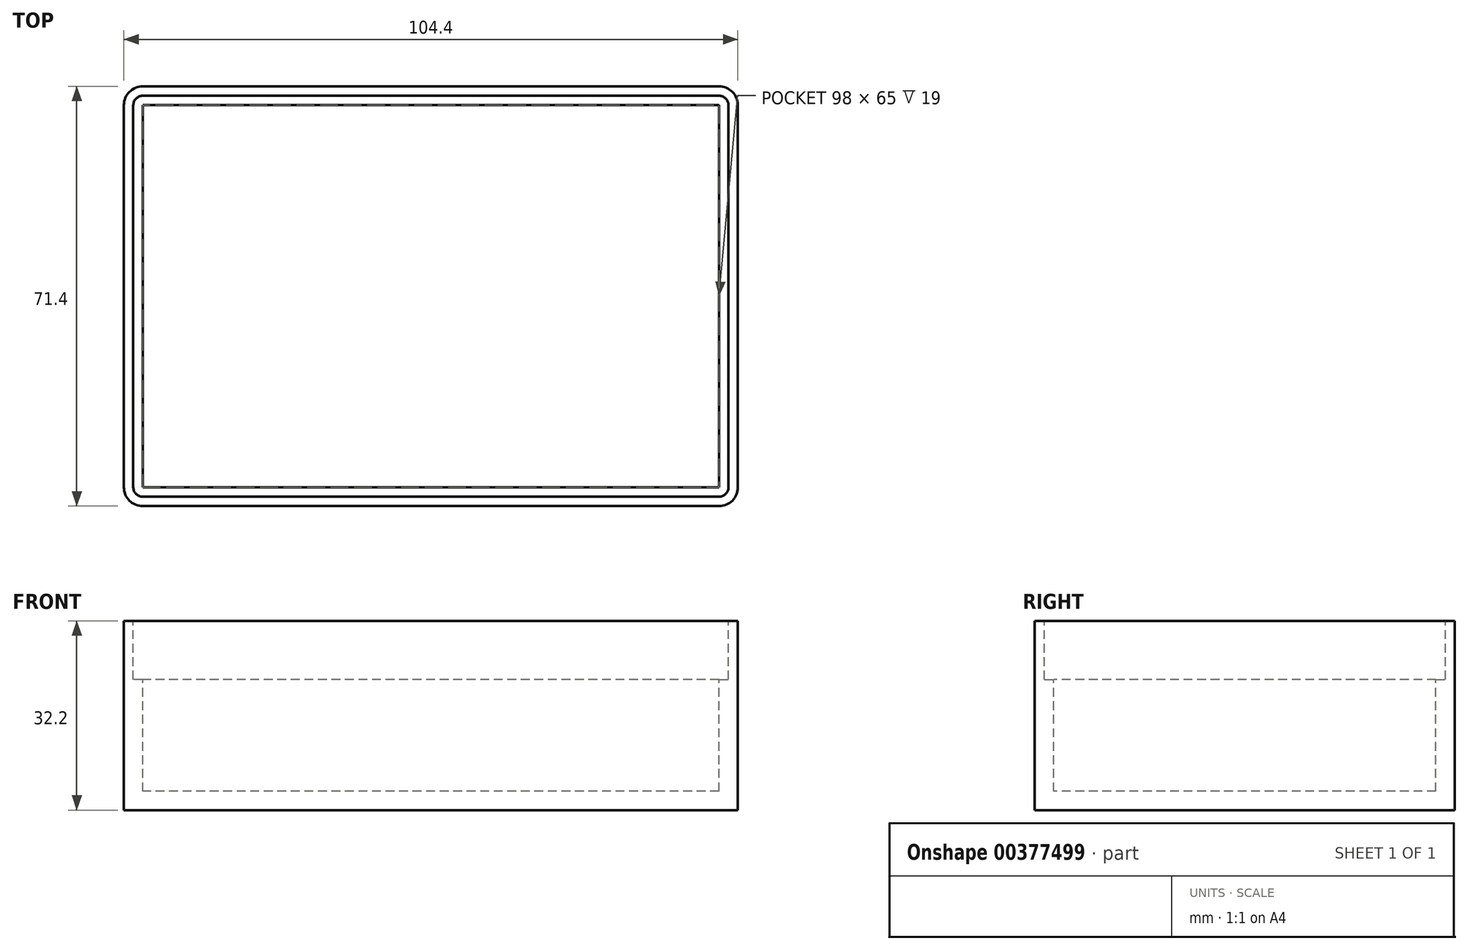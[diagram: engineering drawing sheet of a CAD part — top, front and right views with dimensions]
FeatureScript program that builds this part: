
annotation { "Feature Type Name" : "Feature", "Feature Type Description" : "" }
export const myFeature = defineFeature(function(context is Context, id is Id, definition is map)
    precondition{}
    {
        {
            assignVariable(context, id + "F0", {"name" : "InnerDepth", "anyValue" : 19 * mm});
        }
        {
            assignVariable(context, id + "F1", {"name" : "WallThickness", "anyValue" : 3.2 * mm});
        }
        {
            assignVariable(context, id + "F2", {"name" : "LidDepth", "anyValue" : 10 * mm});
        }
        {
            var Q0;
            Q0=qCreatedBy(makeId("Top.planeOp"),FACE);
            var sketch = newSketch(context, id + "F3", { "sketchPlane" : qUnion([Q0])});
            skLineSegment(sketch, "E0.bottom", {"start": v(52.2, 35.7) * mm, "end": v(-52.2, 35.7) * mm});
            skLineSegment(sketch, "E0.top", {"start": v(52.2, -35.7) * mm, "end": v(-52.2, -35.7) * mm});
            skLineSegment(sketch, "E0.left", {"start": v(52.2, 35.7) * mm, "end": v(52.2, -35.7) * mm});
            skLineSegment(sketch, "E0.right", {"start": v(-52.2, 35.7) * mm, "end": v(-52.2, -35.7) * mm});
            skPoint(sketch, "E0.middle", {"position": v(0, 0) * mm});
            skSolve(sketch);
        }
        {
            var Q0;
            Q0=qCreatedBy(makeId("Top.planeOp"),FACE);
            var sketch = newSketch(context, id + "F4", { "sketchPlane" : qUnion([Q0])});
            skLineSegment(sketch, "E1.bottom", {"start": v(50.6, 34.1) * mm, "end": v(-50.6, 34.1) * mm});
            skLineSegment(sketch, "E1.top", {"start": v(50.6, -34.1) * mm, "end": v(-50.6, -34.1) * mm});
            skLineSegment(sketch, "E1.left", {"start": v(50.6, 34.1) * mm, "end": v(50.6, -34.1) * mm});
            skLineSegment(sketch, "E1.right", {"start": v(-50.6, 34.1) * mm, "end": v(-50.6, -34.1) * mm});
            skPoint(sketch, "E1.middle", {"position": v(0, 0) * mm});
            skSolve(sketch);
        }
        {
            var Q0;
            Q0=qCreatedBy(makeId("Top.planeOp"),FACE);
            var sketch = newSketch(context, id + "F5", { "sketchPlane" : qUnion([Q0])});
            skLineSegment(sketch, "E2.bottom", {"start": v(49, 32.5) * mm, "end": v(-49, 32.5) * mm});
            skLineSegment(sketch, "E2.top", {"start": v(49, -32.5) * mm, "end": v(-49, -32.5) * mm});
            skLineSegment(sketch, "E2.left", {"start": v(49, 32.5) * mm, "end": v(49, -32.5) * mm});
            skLineSegment(sketch, "E2.right", {"start": v(-49, 32.5) * mm, "end": v(-49, -32.5) * mm});
            skPoint(sketch, "E2.middle", {"position": v(0, 0) * mm});
            skSolve(sketch);
        }
        {
            var Q0;
            Q0=makeQuery(id+"F3.imprint","IMPRINT",FACE,{"disambiguationData":[TD([[makeQuery(id+"F3.imprint","IMPRINT",EDGE,{"derivedFrom":sQuery(id+"F3.wireOp",EDGE,"E0.bottom")}),1.0]])]});
            extrude(context, id + "F6", {"entities" : qUnion([Q0]), "oppositeDirection" : true, "depth" : getVariable(context, 'InnerDepth') + getVariable(context, 'LidDepth') + getVariable(context, 'WallThickness')});
        }
        {
            var Q0;
            Q0 = qSketchRegion(id + "F4", true);
            extrude(context, id + "F7", {"entities" : qUnion([Q0]), "operationType" : NewBodyOperationType.REMOVE, "oppositeDirection" : true, "depth" : getVariable(context, 'LidDepth')});
        }
        {
            var Q0;
            Q0 = qSketchRegion(id + "F5", true);
            extrude(context, id + "F8", {"entities" : qUnion([Q0]), "operationType" : NewBodyOperationType.REMOVE, "oppositeDirection" : true, "depth" : getVariable(context, 'LidDepth') + getVariable(context, 'InnerDepth')});
        }
        {
            var Q0;
            Q0=makeQuery(id+"F6.opExtrude","SWEPT_EDGE",EDGE,{"disambiguationData":[OSD([sQuery(id+"F3.wireOp",EDGE,"E0.top"),sQuery(id+"F3.wireOp",EDGE,"E0.right")])]});
            var Q1;
            Q1=makeQuery(id+"F6.opExtrude","SWEPT_EDGE",EDGE,{"disambiguationData":[OSD([sQuery(id+"F3.wireOp",EDGE,"E0.top"),sQuery(id+"F3.wireOp",EDGE,"E0.left")])]});
            var Q2;
            Q2=makeQuery(id+"F6.opExtrude","SWEPT_EDGE",EDGE,{"disambiguationData":[OSD([sQuery(id+"F3.wireOp",EDGE,"E0.bottom"),sQuery(id+"F3.wireOp",EDGE,"E0.left")])]});
            var Q3;
            Q3=makeQuery(id+"F6.opExtrude","SWEPT_EDGE",EDGE,{"disambiguationData":[OSD([sQuery(id+"F3.wireOp",EDGE,"E0.bottom"),sQuery(id+"F3.wireOp",EDGE,"E0.right")])]});
            fillet(context, id + "F9", {"entities" : qUnion([Q0, Q1, Q2, Q3]), "radius" : getVariable(context, 'WallThickness'), "tangentPropagation" : true, "allowEdgeOverflow" : false});
        }
        {
            var Q0;
            Q0=makeQuery(id+"F7.boolean.opBoolean","COPY",EDGE,{"derivedFrom":makeQuery(id+"F7.opExtrude","SWEPT_EDGE",EDGE,{"disambiguationData":[OSD([sQuery(id+"F4.wireOp",EDGE,"E1.bottom"),sQuery(id+"F4.wireOp",EDGE,"E1.right")])]})});
            var Q1;
            Q1=makeQuery(id+"F7.boolean.opBoolean","COPY",EDGE,{"derivedFrom":makeQuery(id+"F7.opExtrude","SWEPT_EDGE",EDGE,{"disambiguationData":[OSD([sQuery(id+"F4.wireOp",EDGE,"E1.top"),sQuery(id+"F4.wireOp",EDGE,"E1.right")])]})});
            var Q2;
            Q2=makeQuery(id+"F7.boolean.opBoolean","COPY",EDGE,{"derivedFrom":makeQuery(id+"F7.opExtrude","SWEPT_EDGE",EDGE,{"disambiguationData":[OSD([sQuery(id+"F4.wireOp",EDGE,"E1.bottom"),sQuery(id+"F4.wireOp",EDGE,"E1.left")])]})});
            var Q3;
            Q3=makeQuery(id+"F7.boolean.opBoolean","COPY",EDGE,{"derivedFrom":makeQuery(id+"F7.opExtrude","SWEPT_EDGE",EDGE,{"disambiguationData":[OSD([sQuery(id+"F4.wireOp",EDGE,"E1.top"),sQuery(id+"F4.wireOp",EDGE,"E1.left")])]})});
            fillet(context, id + "F10", {"entities" : qUnion([Q0, Q1, Q2, Q3]), "radius" : getVariable(context, 'WallThickness') / 2, "tangentPropagation" : true, "allowEdgeOverflow" : false});
        }
    });
